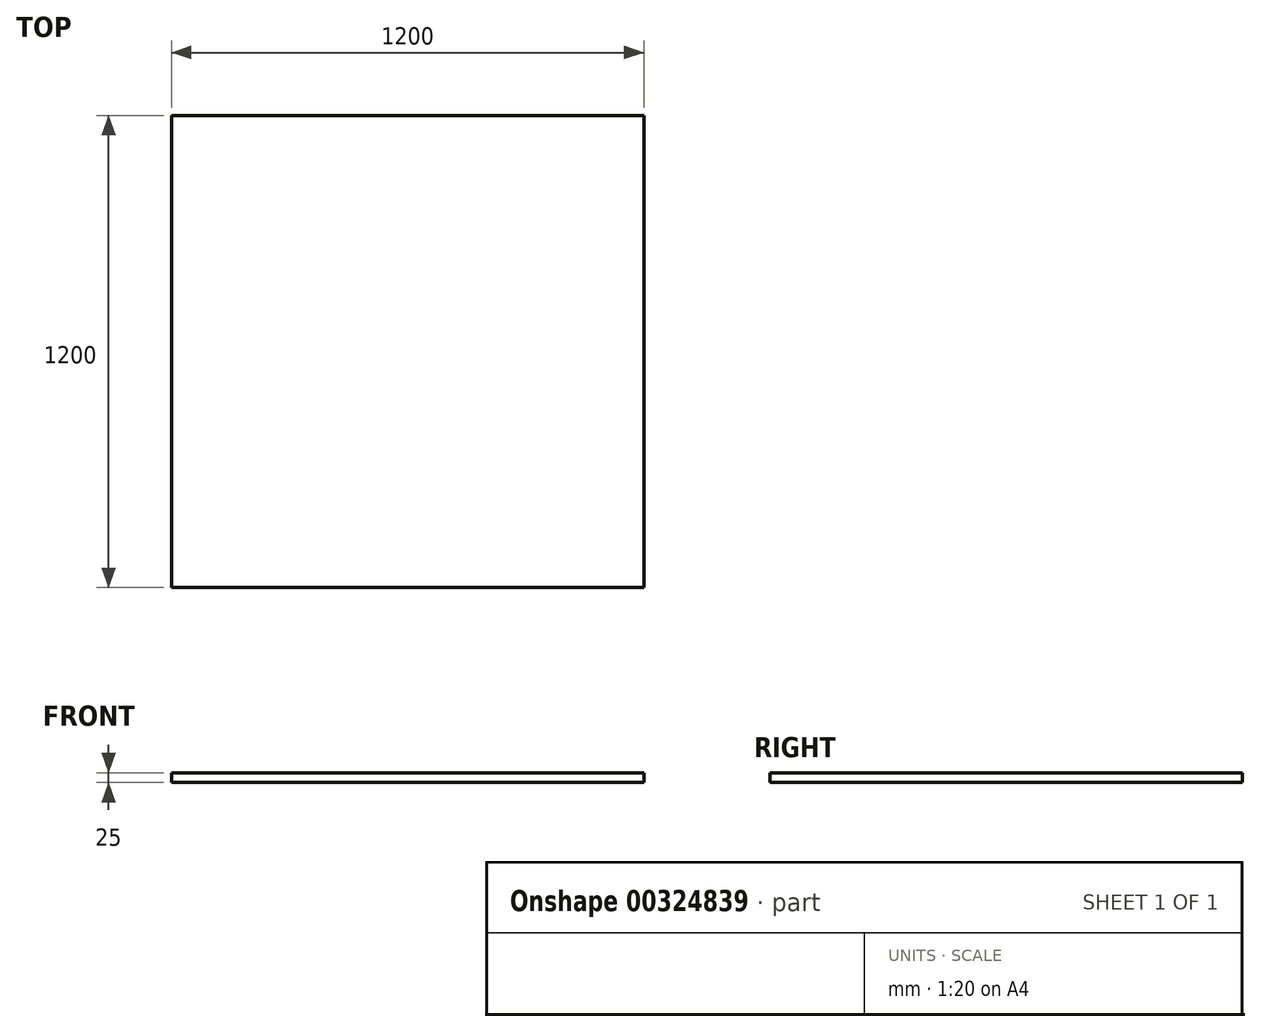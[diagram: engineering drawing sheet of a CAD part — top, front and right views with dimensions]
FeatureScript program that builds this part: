
annotation { "Feature Type Name" : "Feature", "Feature Type Description" : "" }
export const myFeature = defineFeature(function(context is Context, id is Id, definition is map)
    precondition{}
    {
        {
            var Q0;
            Q0=qCreatedBy(makeId("Top.planeOp"),FACE);
            var sketch = newSketch(context, id + "F0", { "sketchPlane" : qUnion([Q0])});
            skLineSegment(sketch, "E0", {"start": v(-563.29, -573.5) * mm, "end": v(437.2, -573.5) * mm});
            skLineSegment(sketch, "E1", {"start": v(437.2, -573.5) * mm, "end": v(437.2, 626.5) * mm});
            skLineSegment(sketch, "E2", {"start": v(437.2, 626.5) * mm, "end": v(-762.8, 626.5) * mm});
            skLineSegment(sketch, "E3", {"start": v(-762.8, 626.5) * mm, "end": v(-762.8, -573.5) * mm});
            skLineSegment(sketch, "E4", {"start": v(-762.8, -573.5) * mm, "end": v(-563.29, -573.5) * mm});
            skLineSegment(sketch, "E5", {"start": v(-63.05, -573.5) * mm, "end": v(183.25, -573.5) * mm});
            skSolve(sketch);
        }
        {
            var Q0;
            Q0 = qSketchRegion(id + "F0", true);
            extrude(context, id + "F1", {"entities" : qUnion([Q0]), "depth" : 25 * mm});
        }
    });
